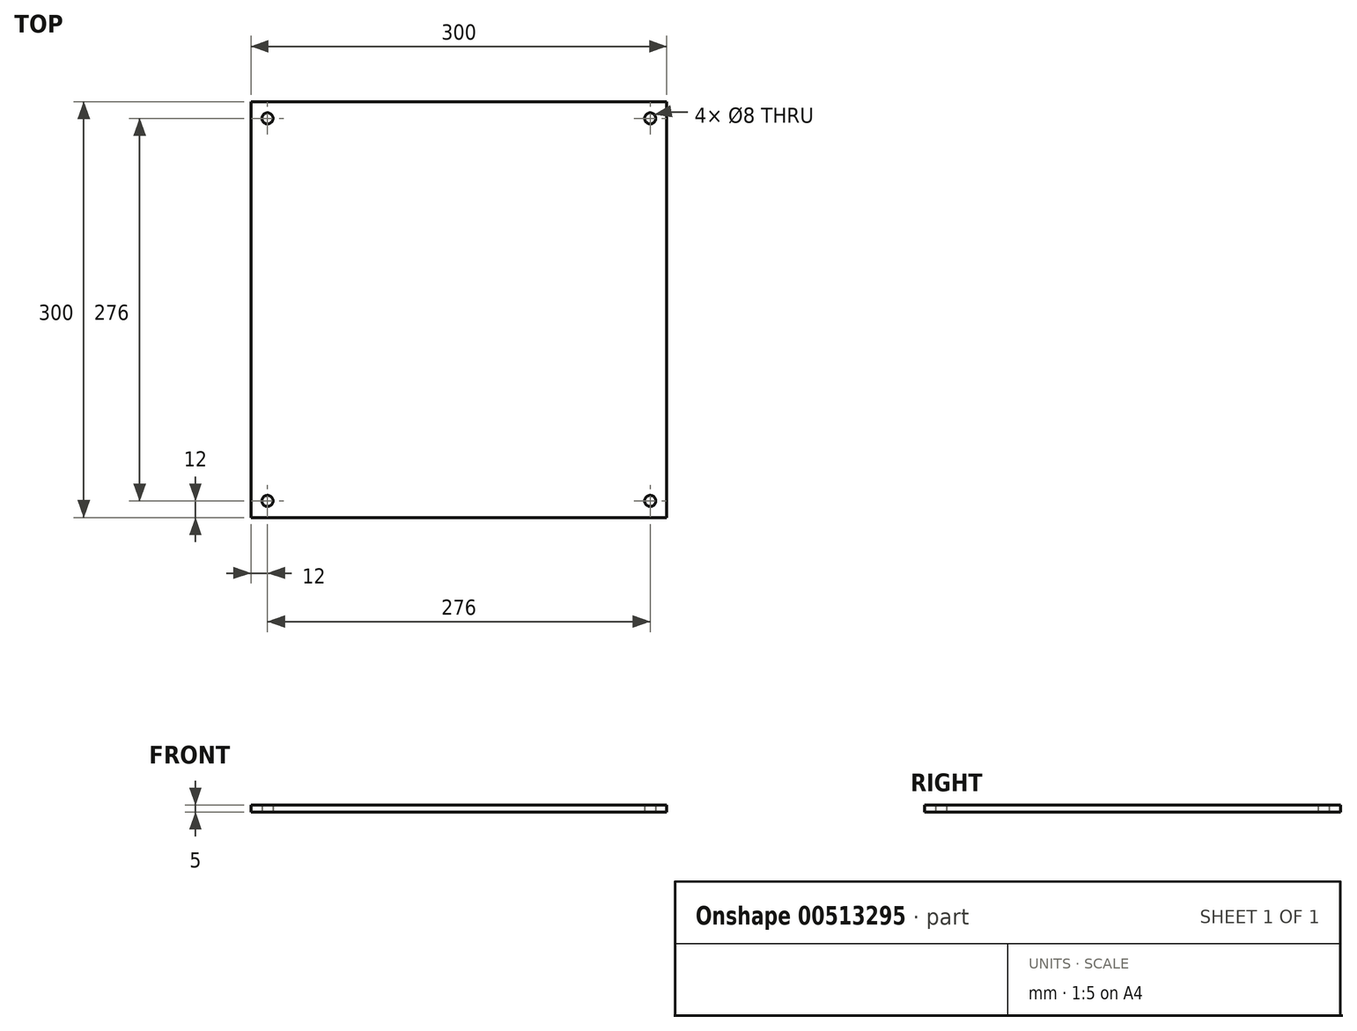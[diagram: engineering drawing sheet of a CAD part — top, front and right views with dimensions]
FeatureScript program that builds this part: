
annotation { "Feature Type Name" : "Feature", "Feature Type Description" : "" }
export const myFeature = defineFeature(function(context is Context, id is Id, definition is map)
    precondition{}
    {
        {
            var Q0;
            Q0=qCreatedBy(makeId("Front.planeOp"),FACE);
            var sketch = newSketch(context, id + "F0", { "sketchPlane" : qUnion([Q0])});
            skLineSegment(sketch, "E0.bottom", {"start": v(-150, 2.5) * mm, "end": v(150, 2.5) * mm});
            skLineSegment(sketch, "E0.top", {"start": v(-150, -2.5) * mm, "end": v(150, -2.5) * mm});
            skLineSegment(sketch, "E0.left", {"start": v(-150, 2.5) * mm, "end": v(-150, -2.5) * mm});
            skLineSegment(sketch, "E0.right", {"start": v(150, 2.5) * mm, "end": v(150, -2.5) * mm});
            skPoint(sketch, "E0.middle", {"position": v(0, 0) * mm});
            skLineSegment(sketch, "E1.left", {"start": v(-150, 2.5) * mm, "end": v(-150, 2.5) * mm});
            skLineSegment(sketch, "E1.right", {"start": v(150, 2.5) * mm, "end": v(150, 2.5) * mm});
            skSolve(sketch);
        }
        {
            var Q0;
            Q0 = qSketchRegion(id + "F0", true);
            extrude(context, id + "F1", {"entities" : qUnion([Q0]), "endBound" : BoundingType.SYMMETRIC, "depth" : 300 * mm});
        }
        {
            var Q0;
            Q0=qCreatedBy(makeId("Top.planeOp"),FACE);
            var sketch = newSketch(context, id + "F2", { "sketchPlane" : qUnion([Q0])});
            skCircle(sketch, "E2", {"center": v(138, -138) * mm, "radius": 4 * mm});
            skCircle(sketch, "E3.MirrorC", {"center": v(-138, -138) * mm, "radius": 4 * mm});
            skCircle(sketch, "E4.MirrorC", {"center": v(-138, 138) * mm, "radius": 4 * mm});
            skCircle(sketch, "E5.MirrorC", {"center": v(138, 138) * mm, "radius": 4 * mm});
            skSolve(sketch);
        }
        {
            var Q0;
            Q0 = qSketchRegion(id + "F2", true);
            extrude(context, id + "F3", {"entities" : qUnion([Q0]), "operationType" : NewBodyOperationType.REMOVE, "endBound" : BoundingType.SYMMETRIC, "depth" : 6 * mm});
        }
    });
